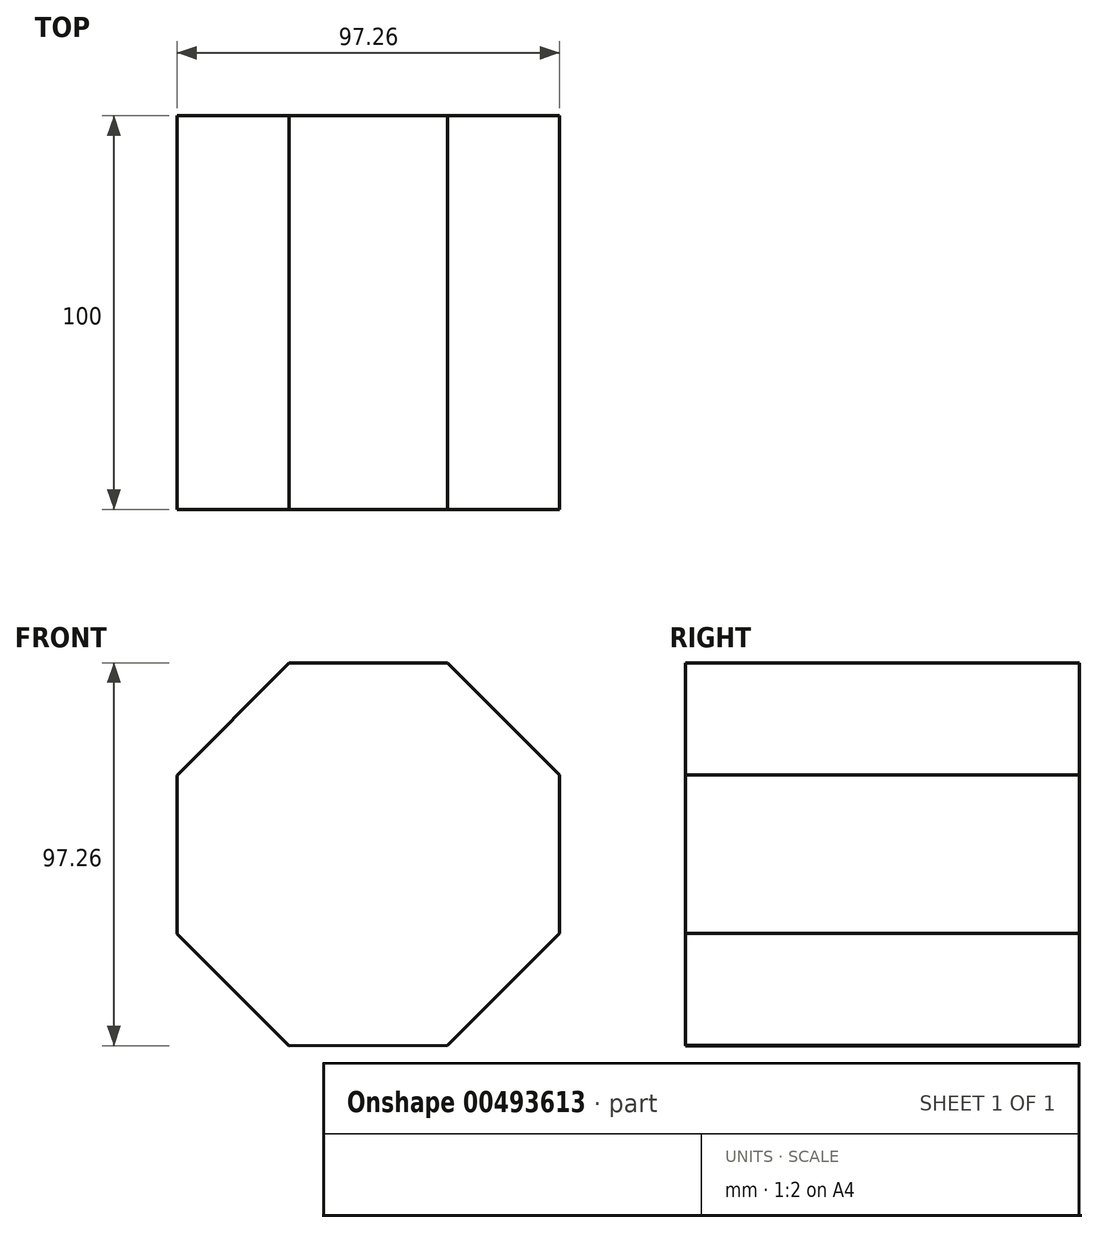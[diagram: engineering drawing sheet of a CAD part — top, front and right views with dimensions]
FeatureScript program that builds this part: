
annotation { "Feature Type Name" : "Feature", "Feature Type Description" : "" }
export const myFeature = defineFeature(function(context is Context, id is Id, definition is map)
    precondition{}
    {
        {
            var Q0;
            Q0=qCreatedBy(makeId("Front.planeOp"),FACE);
            var sketch = newSketch(context, id + "F0", { "sketchPlane" : qUnion([Q0])});
            skCircle(sketch, "E0.cCircle", {"center": v(0, 0) * mm, "radius": 52.61 * mm, "construction": true});
            skLineSegment(sketch, "E0.0", {"start": v(-48.58, -20.18) * mm, "end": v(-48.63, 20.08) * mm});
            skLineSegment(sketch, "E0.1", {"start": v(-48.63, 20.08) * mm, "end": v(-20.18, 48.58) * mm});
            skLineSegment(sketch, "E0.2", {"start": v(-20.18, 48.58) * mm, "end": v(20.08, 48.63) * mm});
            skLineSegment(sketch, "E0.3", {"start": v(20.08, 48.63) * mm, "end": v(48.58, 20.18) * mm});
            skLineSegment(sketch, "E0.4", {"start": v(48.58, 20.18) * mm, "end": v(48.63, -20.08) * mm});
            skLineSegment(sketch, "E0.5", {"start": v(48.63, -20.08) * mm, "end": v(20.18, -48.58) * mm});
            skLineSegment(sketch, "E0.6", {"start": v(20.18, -48.58) * mm, "end": v(-20.08, -48.63) * mm});
            skLineSegment(sketch, "E0.7", {"start": v(-20.08, -48.63) * mm, "end": v(-48.58, -20.18) * mm});
            skSolve(sketch);
        }
        {
            var Q0;
            Q0=makeQuery(id+"F0.imprint","IMPRINT",FACE,{"disambiguationData":[TD([[makeQuery(id+"F0.imprint","IMPRINT",EDGE,{"derivedFrom":sQuery(id+"F0.wireOp",EDGE,"E0.0")}),-1.0]])]});
            extrude(context, id + "F1", {"entities" : qUnion([Q0]), "depth" : 100 * mm});
        }
    });
